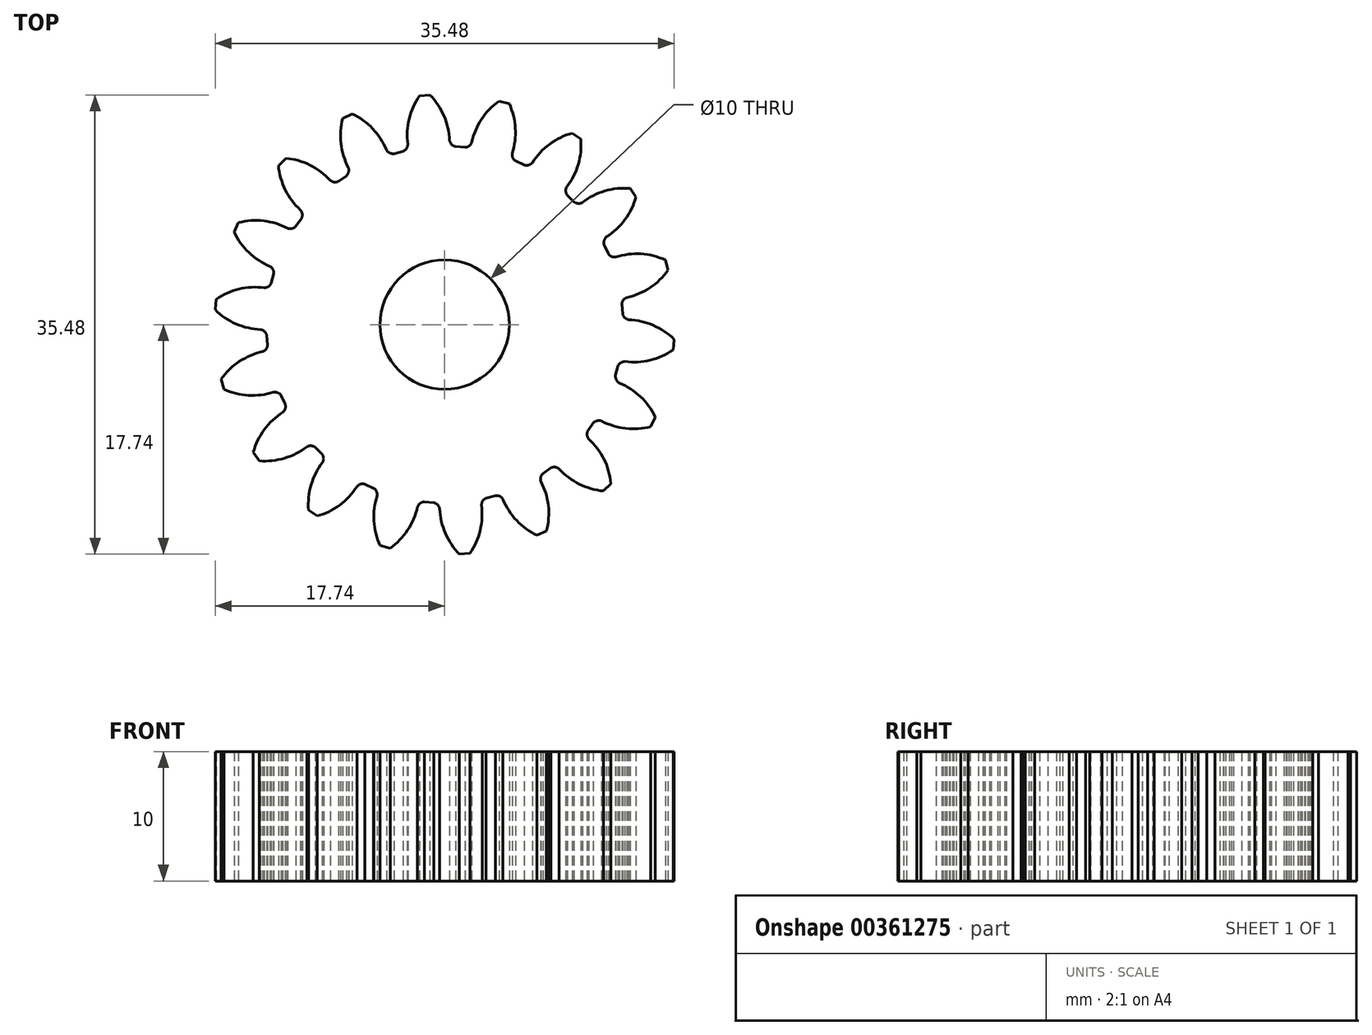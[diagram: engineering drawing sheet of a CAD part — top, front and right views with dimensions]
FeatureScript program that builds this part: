
annotation { "Feature Type Name" : "Feature", "Feature Type Description" : "" }
export const myFeature = defineFeature(function(context is Context, id is Id, definition is map)
    precondition{}
    {
        {
            var Q0;
            Q0=qCreatedBy(makeId("Top.planeOp"),FACE);
            var sketch = newSketch(context, id + "F0", { "sketchPlane" : qUnion([Q0])});
            skLineSegment(sketch, "E0", {"start": v(0, 0) * mm, "end": v(0, 32) * mm, "construction": true});
            skCircle(sketch, "E1", {"center": v(0, 0) * mm, "radius": 16 * mm, "construction": true});
            skCircle(sketch, "E2", {"center": v(0, 32) * mm, "radius": 16 * mm, "construction": true});
            skCircle(sketch, "E3", {"center": v(0, 0) * mm, "radius": 13.78 * mm, "construction": true});
            skCircle(sketch, "E4", {"center": v(0, 32) * mm, "radius": 13.78 * mm, "construction": true});
            skCircle(sketch, "E5", {"center": v(0, 0) * mm, "radius": 17.78 * mm, "construction": true});
            skCircle(sketch, "E6", {"center": v(0, 32) * mm, "radius": 17.78 * mm, "construction": true});
            skLineSegment(sketch, "E7", {"start": v(0, 16) * mm, "end": v(-30.4, 16) * mm, "construction": true});
            skLineSegment(sketch, "E8", {"start": v(0, 16) * mm, "end": v(-28.6, 5.59) * mm, "construction": true});
            skLineSegment(sketch, "E9", {"start": v(0, 16) * mm, "end": v(28.87, 26.5) * mm, "construction": true});
            skCircle(sketch, "E10", {"center": v(0, 32) * mm, "radius": 15.05 * mm, "construction": true});
            skCircle(sketch, "E11", {"center": v(0, 32) * mm, "radius": 17 * mm, "construction": true});
            skCircle(sketch, "E12", {"center": v(0, 0) * mm, "radius": 17 * mm, "construction": true});
            skCircle(sketch, "E13", {"center": v(0, 0) * mm, "radius": 15.05 * mm, "construction": true});
            skLineSegment(sketch, "E14", {"start": v(0, 0) * mm, "end": v(-3.73, 14.64) * mm, "construction": true});
            skLineSegment(sketch, "E15", {"start": v(-3.73, 14.64) * mm, "end": v(-2.95, 12.49) * mm, "construction": true});
            skLineSegment(sketch, "E16", {"start": v(-0.18, 16.5) * mm, "end": v(0.18, 15.5) * mm, "construction": true});
            skLineSegment(sketch, "E17", {"start": v(-6.25, 13.73) * mm, "end": v(0, 0) * mm, "construction": true});
            skLineSegment(sketch, "E18", {"start": v(-6.25, 13.73) * mm, "end": v(-3.81, 10.36) * mm, "construction": true});
            skLineSegment(sketch, "E19", {"start": v(0, 0) * mm, "end": v(0.18, 15.5) * mm, "construction": true});
            skLineSegment(sketch, "E20", {"start": v(0.18, 15.5) * mm, "end": v(0.99, 11.26) * mm, "construction": true});
            skLineSegment(sketch, "E21", {"start": v(0.36, 14.58) * mm, "end": v(0, 0) * mm, "construction": true});
            skLineSegment(sketch, "E22", {"start": v(0.36, 14.58) * mm, "end": v(0.61, 11.2) * mm, "construction": true});
            skLineSegment(sketch, "E23", {"start": v(0, 0) * mm, "end": v(4.85, 17.75) * mm, "construction": true});
            skLineSegment(sketch, "E24", {"start": v(4.85, 17.75) * mm, "end": v(3.87, 20.46) * mm, "construction": true});
            skLineSegment(sketch, "E25", {"start": v(0, 0) * mm, "end": v(-0.18, 16.5) * mm, "construction": true});
            skLineSegment(sketch, "E26", {"start": v(-0.18, 16.5) * mm, "end": v(-2.53, 19.74) * mm, "construction": true});
            skLineSegment(sketch, "E27", {"start": v(-0.18, 16.5) * mm, "end": v(-0.8, 17.37) * mm, "construction": true});
            skArc(sketch, "E28.trimOffspring", {"start": v(-5.42, 14.04) * mm, "mid": v(-5.42, 14.03) * mm, "end": v(-5.42, 14.03) * mm});
            skCircle(sketch, "E29", {"center": v(0, 16) * mm, "radius": 1.4 * mm, "construction": true});
            skLineSegment(sketch, "E30", {"start": v(-1.4, 15.94) * mm, "end": v(0, 0) * mm, "construction": true});
            skArc(sketch, "E31.trimOffspring", {"start": v(0.38, 13.77) * mm, "mid": v(0.03, 15.92) * mm, "end": v(-1.15, 17.74) * mm});
            skArc(sketch, "E32.MirrorCS", {"start": v(-2.77, 13.5) * mm, "mid": v(-2.8, 15.67) * mm, "end": v(-1.95, 17.67) * mm});
            skLineSegment(sketch, "E33", {"start": v(-1.95, 17.67) * mm, "end": v(-1.15, 17.74) * mm});
            skLineSegment(sketch, "E34.1.0", {"start": v(-7.88, 15.94) * mm, "end": v(-7.15, 16.28) * mm});
            skArc(sketch, "E34.1.1", {"start": v(-4.35, 13.08) * mm, "mid": v(-5.41, 14.97) * mm, "end": v(-7.15, 16.28) * mm});
            skArc(sketch, "E34.1.2", {"start": v(-7.22, 11.74) * mm, "mid": v(-7.99, 13.77) * mm, "end": v(-7.88, 15.94) * mm});
            skLineSegment(sketch, "E34.2.0", {"start": v(-12.85, 12.28) * mm, "end": v(-12.28, 12.85) * mm});
            skArc(sketch, "E34.2.1", {"start": v(-8.56, 10.8) * mm, "mid": v(-10.2, 12.21) * mm, "end": v(-12.28, 12.85) * mm});
            skArc(sketch, "E34.2.2", {"start": v(-10.8, 8.56) * mm, "mid": v(-12.21, 10.2) * mm, "end": v(-12.85, 12.28) * mm});
            skLineSegment(sketch, "E34.3.0", {"start": v(-16.28, 7.15) * mm, "end": v(-15.94, 7.88) * mm});
            skArc(sketch, "E34.3.1", {"start": v(-11.74, 7.22) * mm, "mid": v(-13.77, 7.99) * mm, "end": v(-15.94, 7.88) * mm});
            skArc(sketch, "E34.3.2", {"start": v(-13.07, 4.35) * mm, "mid": v(-14.97, 5.42) * mm, "end": v(-16.28, 7.15) * mm});
            skLineSegment(sketch, "E34.4.0", {"start": v(-17.74, 1.15) * mm, "end": v(-17.67, 1.95) * mm});
            skArc(sketch, "E34.4.1", {"start": v(-13.5, 2.77) * mm, "mid": v(-15.67, 2.8) * mm, "end": v(-17.67, 1.95) * mm});
            skArc(sketch, "E34.4.2", {"start": v(-13.77, -0.38) * mm, "mid": v(-15.92, -0.03) * mm, "end": v(-17.74, 1.15) * mm});
            skLineSegment(sketch, "E34.5.0", {"start": v(-17.07, -4.99) * mm, "end": v(-17.27, -4.21) * mm});
            skArc(sketch, "E34.5.1", {"start": v(-13.63, -2.01) * mm, "mid": v(-15.68, -2.73) * mm, "end": v(-17.27, -4.21) * mm});
            skArc(sketch, "E34.5.2", {"start": v(-12.81, -5.07) * mm, "mid": v(-14.95, -5.47) * mm, "end": v(-17.07, -4.99) * mm});
            skLineSegment(sketch, "E34.6.0", {"start": v(-14.33, -10.53) * mm, "end": v(-14.8, -9.86) * mm});
            skArc(sketch, "E34.6.1", {"start": v(-12.12, -6.56) * mm, "mid": v(-13.8, -7.93) * mm, "end": v(-14.8, -9.86) * mm});
            skArc(sketch, "E34.6.2", {"start": v(-10.3, -9.15) * mm, "mid": v(-12.17, -10.26) * mm, "end": v(-14.33, -10.53) * mm});
            skLineSegment(sketch, "E34.7.0", {"start": v(-9.87, -14.8) * mm, "end": v(-10.53, -14.33) * mm});
            skArc(sketch, "E34.7.1", {"start": v(-9.15, -10.3) * mm, "mid": v(-10.26, -12.17) * mm, "end": v(-10.53, -14.33) * mm});
            skArc(sketch, "E34.7.2", {"start": v(-6.56, -12.12) * mm, "mid": v(-7.93, -13.8) * mm, "end": v(-9.87, -14.8) * mm});
            skLineSegment(sketch, "E34.8.0", {"start": v(-4.21, -17.27) * mm, "end": v(-5, -17.07) * mm});
            skArc(sketch, "E34.8.1", {"start": v(-5.07, -12.81) * mm, "mid": v(-5.47, -14.95) * mm, "end": v(-5, -17.07) * mm});
            skArc(sketch, "E34.8.2", {"start": v(-2.02, -13.63) * mm, "mid": v(-2.73, -15.68) * mm, "end": v(-4.21, -17.27) * mm});
            skLineSegment(sketch, "E34.9.0", {"start": v(1.95, -17.67) * mm, "end": v(1.15, -17.74) * mm});
            skArc(sketch, "E34.9.1", {"start": v(-0.38, -13.77) * mm, "mid": v(-0.03, -15.92) * mm, "end": v(1.15, -17.74) * mm});
            skArc(sketch, "E34.9.2", {"start": v(2.77, -13.5) * mm, "mid": v(2.8, -15.67) * mm, "end": v(1.95, -17.67) * mm});
            skLineSegment(sketch, "E34.10.0", {"start": v(7.88, -15.94) * mm, "end": v(7.15, -16.28) * mm});
            skArc(sketch, "E34.10.1", {"start": v(4.35, -13.08) * mm, "mid": v(5.41, -14.97) * mm, "end": v(7.15, -16.28) * mm});
            skArc(sketch, "E34.10.2", {"start": v(7.22, -11.74) * mm, "mid": v(7.99, -13.77) * mm, "end": v(7.88, -15.94) * mm});
            skLineSegment(sketch, "E34.11.0", {"start": v(12.85, -12.28) * mm, "end": v(12.28, -12.85) * mm});
            skArc(sketch, "E34.11.1", {"start": v(8.56, -10.8) * mm, "mid": v(10.2, -12.21) * mm, "end": v(12.28, -12.85) * mm});
            skArc(sketch, "E34.11.2", {"start": v(10.8, -8.56) * mm, "mid": v(12.21, -10.2) * mm, "end": v(12.85, -12.28) * mm});
            skLineSegment(sketch, "E34.12.0", {"start": v(16.28, -7.15) * mm, "end": v(15.94, -7.88) * mm});
            skArc(sketch, "E34.12.1", {"start": v(11.74, -7.22) * mm, "mid": v(13.77, -7.99) * mm, "end": v(15.94, -7.88) * mm});
            skArc(sketch, "E34.12.2", {"start": v(13.07, -4.35) * mm, "mid": v(14.97, -5.42) * mm, "end": v(16.28, -7.15) * mm});
            skLineSegment(sketch, "E34.13.0", {"start": v(17.74, -1.15) * mm, "end": v(17.67, -1.95) * mm});
            skArc(sketch, "E34.13.1", {"start": v(13.5, -2.77) * mm, "mid": v(15.67, -2.8) * mm, "end": v(17.67, -1.95) * mm});
            skArc(sketch, "E34.13.2", {"start": v(13.77, 0.38) * mm, "mid": v(15.92, 0.03) * mm, "end": v(17.74, -1.15) * mm});
            skLineSegment(sketch, "E34.14.0", {"start": v(17.07, 4.99) * mm, "end": v(17.27, 4.21) * mm});
            skArc(sketch, "E34.14.1", {"start": v(13.63, 2.01) * mm, "mid": v(15.68, 2.73) * mm, "end": v(17.27, 4.21) * mm});
            skArc(sketch, "E34.14.2", {"start": v(12.81, 5.07) * mm, "mid": v(14.95, 5.47) * mm, "end": v(17.07, 4.99) * mm});
            skLineSegment(sketch, "E34.15.0", {"start": v(14.33, 10.53) * mm, "end": v(14.8, 9.86) * mm});
            skArc(sketch, "E34.15.1", {"start": v(12.12, 6.56) * mm, "mid": v(13.8, 7.93) * mm, "end": v(14.8, 9.86) * mm});
            skArc(sketch, "E34.15.2", {"start": v(10.3, 9.15) * mm, "mid": v(12.17, 10.26) * mm, "end": v(14.33, 10.53) * mm});
            skLineSegment(sketch, "E34.16.0", {"start": v(9.87, 14.8) * mm, "end": v(10.53, 14.33) * mm});
            skArc(sketch, "E34.16.1", {"start": v(9.15, 10.3) * mm, "mid": v(10.26, 12.17) * mm, "end": v(10.53, 14.33) * mm});
            skArc(sketch, "E34.16.2", {"start": v(6.56, 12.12) * mm, "mid": v(7.93, 13.8) * mm, "end": v(9.87, 14.8) * mm});
            skLineSegment(sketch, "E34.17.0", {"start": v(4.21, 17.27) * mm, "end": v(5, 17.07) * mm});
            skArc(sketch, "E34.17.1", {"start": v(5.07, 12.81) * mm, "mid": v(5.47, 14.95) * mm, "end": v(5, 17.07) * mm});
            skArc(sketch, "E34.17.2", {"start": v(2.02, 13.63) * mm, "mid": v(2.73, 15.68) * mm, "end": v(4.21, 17.27) * mm});
            skCircle(sketch, "E35", {"center": v(0.38, 13.77) * mm, "radius": 0.45 * mm, "construction": true});
            skCircle(sketch, "E36", {"center": v(2.02, 13.63) * mm, "radius": 0.45 * mm, "construction": true});
            skArc(sketch, "E37", {"start": v(0.38, 14.22) * mm, "mid": v(0.54, 13.92) * mm, "end": v(0.83, 13.75) * mm});
            skArc(sketch, "E38", {"start": v(1.57, 13.7) * mm, "mid": v(1.89, 13.8) * mm, "end": v(2.1, 14.08) * mm});
            skLineSegment(sketch, "E39", {"start": v(0.83, 13.75) * mm, "end": v(1.57, 13.7) * mm});
            skArc(sketch, "E40.1.0", {"start": v(-4.5, 13.5) * mm, "mid": v(-4.25, 13.27) * mm, "end": v(-3.92, 13.21) * mm});
            skArc(sketch, "E40.1.1", {"start": v(-3.2, 13.4) * mm, "mid": v(-2.95, 13.62) * mm, "end": v(-2.85, 13.94) * mm});
            skLineSegment(sketch, "E40.1.2", {"start": v(-3.92, 13.21) * mm, "end": v(-3.2, 13.4) * mm});
            skArc(sketch, "E40.2.0", {"start": v(-8.85, 11.14) * mm, "mid": v(-8.54, 11.01) * mm, "end": v(-8.2, 11.07) * mm});
            skArc(sketch, "E40.2.1", {"start": v(-7.6, 11.5) * mm, "mid": v(-7.43, 11.79) * mm, "end": v(-7.44, 12.13) * mm});
            skLineSegment(sketch, "E40.2.2", {"start": v(-8.2, 11.07) * mm, "end": v(-7.6, 11.5) * mm});
            skArc(sketch, "E40.3.0", {"start": v(-12.13, 7.44) * mm, "mid": v(-11.79, 7.43) * mm, "end": v(-11.5, 7.6) * mm});
            skArc(sketch, "E40.3.1", {"start": v(-11.07, 8.2) * mm, "mid": v(-11.01, 8.54) * mm, "end": v(-11.14, 8.85) * mm});
            skLineSegment(sketch, "E40.3.2", {"start": v(-11.5, 7.6) * mm, "end": v(-11.07, 8.2) * mm});
            skArc(sketch, "E40.4.0", {"start": v(-13.94, 2.85) * mm, "mid": v(-13.62, 2.95) * mm, "end": v(-13.4, 3.21) * mm});
            skArc(sketch, "E40.4.1", {"start": v(-13.21, 3.92) * mm, "mid": v(-13.27, 4.26) * mm, "end": v(-13.5, 4.5) * mm});
            skLineSegment(sketch, "E40.4.2", {"start": v(-13.4, 3.21) * mm, "end": v(-13.21, 3.92) * mm});
            skArc(sketch, "E40.5.0", {"start": v(-14.07, -2.1) * mm, "mid": v(-13.8, -1.89) * mm, "end": v(-13.7, -1.57) * mm});
            skArc(sketch, "E40.5.1", {"start": v(-13.75, -0.83) * mm, "mid": v(-13.92, -0.54) * mm, "end": v(-14.23, -0.38) * mm});
            skLineSegment(sketch, "E40.5.2", {"start": v(-13.7, -1.57) * mm, "end": v(-13.75, -0.83) * mm});
            skArc(sketch, "E40.6.0", {"start": v(-12.51, -6.78) * mm, "mid": v(-12.33, -6.5) * mm, "end": v(-12.33, -6.15) * mm});
            skArc(sketch, "E40.6.1", {"start": v(-12.64, -5.49) * mm, "mid": v(-12.9, -5.27) * mm, "end": v(-13.24, -5.22) * mm});
            skLineSegment(sketch, "E40.6.2", {"start": v(-12.33, -6.15) * mm, "end": v(-12.64, -5.49) * mm});
            skArc(sketch, "E40.7.0", {"start": v(-9.44, -10.65) * mm, "mid": v(-9.36, -10.32) * mm, "end": v(-9.48, -10) * mm});
            skArc(sketch, "E40.7.1", {"start": v(-10, -9.48) * mm, "mid": v(-10.32, -9.36) * mm, "end": v(-10.65, -9.44) * mm});
            skLineSegment(sketch, "E40.7.2", {"start": v(-9.48, -10) * mm, "end": v(-10, -9.48) * mm});
            skArc(sketch, "E40.8.0", {"start": v(-5.23, -13.23) * mm, "mid": v(-5.27, -12.9) * mm, "end": v(-5.49, -12.64) * mm});
            skArc(sketch, "E40.8.1", {"start": v(-6.16, -12.33) * mm, "mid": v(-6.5, -12.33) * mm, "end": v(-6.78, -12.51) * mm});
            skLineSegment(sketch, "E40.8.2", {"start": v(-5.49, -12.64) * mm, "end": v(-6.16, -12.33) * mm});
            skArc(sketch, "E40.9.0", {"start": v(-0.38, -14.22) * mm, "mid": v(-0.54, -13.92) * mm, "end": v(-0.83, -13.75) * mm});
            skArc(sketch, "E40.9.1", {"start": v(-1.57, -13.7) * mm, "mid": v(-1.89, -13.8) * mm, "end": v(-2.1, -14.08) * mm});
            skLineSegment(sketch, "E40.9.2", {"start": v(-0.83, -13.75) * mm, "end": v(-1.57, -13.7) * mm});
            skArc(sketch, "E40.10.0", {"start": v(4.5, -13.5) * mm, "mid": v(4.25, -13.27) * mm, "end": v(3.92, -13.21) * mm});
            skArc(sketch, "E40.10.1", {"start": v(3.2, -13.4) * mm, "mid": v(2.95, -13.62) * mm, "end": v(2.85, -13.94) * mm});
            skLineSegment(sketch, "E40.10.2", {"start": v(3.92, -13.21) * mm, "end": v(3.2, -13.4) * mm});
            skArc(sketch, "E40.11.0", {"start": v(8.85, -11.14) * mm, "mid": v(8.54, -11.01) * mm, "end": v(8.2, -11.07) * mm});
            skArc(sketch, "E40.11.1", {"start": v(7.6, -11.5) * mm, "mid": v(7.43, -11.79) * mm, "end": v(7.44, -12.13) * mm});
            skLineSegment(sketch, "E40.11.2", {"start": v(8.2, -11.07) * mm, "end": v(7.6, -11.5) * mm});
            skArc(sketch, "E40.12.0", {"start": v(12.13, -7.44) * mm, "mid": v(11.79, -7.43) * mm, "end": v(11.5, -7.6) * mm});
            skArc(sketch, "E40.12.1", {"start": v(11.07, -8.2) * mm, "mid": v(11.01, -8.54) * mm, "end": v(11.14, -8.85) * mm});
            skLineSegment(sketch, "E40.12.2", {"start": v(11.5, -7.6) * mm, "end": v(11.07, -8.2) * mm});
            skArc(sketch, "E40.13.0", {"start": v(13.94, -2.85) * mm, "mid": v(13.62, -2.95) * mm, "end": v(13.4, -3.21) * mm});
            skArc(sketch, "E40.13.1", {"start": v(13.21, -3.92) * mm, "mid": v(13.27, -4.26) * mm, "end": v(13.5, -4.5) * mm});
            skLineSegment(sketch, "E40.13.2", {"start": v(13.4, -3.21) * mm, "end": v(13.21, -3.92) * mm});
            skArc(sketch, "E40.14.0", {"start": v(14.07, 2.1) * mm, "mid": v(13.8, 1.89) * mm, "end": v(13.7, 1.57) * mm});
            skArc(sketch, "E40.14.1", {"start": v(13.75, 0.83) * mm, "mid": v(13.92, 0.54) * mm, "end": v(14.23, 0.38) * mm});
            skLineSegment(sketch, "E40.14.2", {"start": v(13.7, 1.57) * mm, "end": v(13.75, 0.83) * mm});
            skArc(sketch, "E40.15.0", {"start": v(12.51, 6.78) * mm, "mid": v(12.33, 6.5) * mm, "end": v(12.33, 6.15) * mm});
            skArc(sketch, "E40.15.1", {"start": v(12.64, 5.49) * mm, "mid": v(12.9, 5.27) * mm, "end": v(13.24, 5.22) * mm});
            skLineSegment(sketch, "E40.15.2", {"start": v(12.33, 6.15) * mm, "end": v(12.64, 5.49) * mm});
            skArc(sketch, "E40.16.0", {"start": v(9.44, 10.65) * mm, "mid": v(9.36, 10.32) * mm, "end": v(9.48, 10) * mm});
            skArc(sketch, "E40.16.1", {"start": v(10, 9.48) * mm, "mid": v(10.32, 9.36) * mm, "end": v(10.65, 9.44) * mm});
            skLineSegment(sketch, "E40.16.2", {"start": v(9.48, 10) * mm, "end": v(10, 9.48) * mm});
            skArc(sketch, "E40.17.0", {"start": v(5.23, 13.23) * mm, "mid": v(5.27, 12.9) * mm, "end": v(5.49, 12.64) * mm});
            skArc(sketch, "E40.17.1", {"start": v(6.16, 12.33) * mm, "mid": v(6.5, 12.33) * mm, "end": v(6.78, 12.51) * mm});
            skLineSegment(sketch, "E40.17.2", {"start": v(5.49, 12.64) * mm, "end": v(6.16, 12.33) * mm});
            skCircle(sketch, "E41", {"center": v(0, 0) * mm, "radius": 5 * mm});
            skLineSegment(sketch, "E42", {"start": v(-9.42, 11.47) * mm, "end": v(0, 0) * mm, "construction": true});
            skSolve(sketch);
        }
        {
            var Q0;
            {var subQ56=sQuery(id+"F0.wireOp",EDGE,"E33");Q0=makeQuery(id+"F0.imprint","IMPRINT",FACE,{"disambiguationData":[TD([[makeQuery(id+"F0.imprint","IMPRINT",EDGE,{"derivedFrom":subQ56}),-1.0]])]});}
            extrude(context, id + "F1", {"entities" : qUnion([Q0]), "depth" : 10 * mm});
        }
    });
